# Revit family: Plumbing_Joints_Aignep_Ball-Valve-Tube-90700
name_source: partatom
category: Pipe Accessories
revit_build: Autodesk Revit 2018 (Build: 20170223_1515(x64)
units: mm (PartAtom-declared; Revit-internal decimal feet)

## family parameters
Always vertical = Yes
Cut with Voids When Loaded = No
OmniClass Number = 23.27.43.00
Part Type = Valve - Breaks Into
Round Connector Dimension = Use Diameter
Shared = No
Work Plane-Based = No

## types (6) — shared parameters
Assembly Code = D2040100
BIMobject category = Joints
Description = Ball valve tube/tube
Design country = Italy
Edition number = 1
IFC Classification = Pipe Fitting
Keynote = 15410
Lookup Table Name = Ball Valve Tube- 90705
Manufacturer = Aignep Spa
Manufacturer country = Italy
Manufacturer name = Aignep Spa
Material main = Brass
Material secondary = Aluminium
Model = 90700
OmniClass Code = 23-27 43 00
OmniClass Description = Pipe Fittings
Product Guid = ee17b265-a323-4521-a86a-9f603f37fb54
Product SKU = Ball-Valve-Tube_Tube-90700
Product certification = https://www.aignep.com
Product data url = https://www.bimobject.com
Product family = INFINITY
Product group = Valves
Product name = Ball Valve Tube/Tube- 90700
Product url = https://www.aignep.com
URL = https://www.aignep.com

## per-type parameters (varying)
- D 20: B=31.5 mm; C=58.5 mm; CH1=32 mm; CH2=30 mm; E=34.5 mm; G=88 mm; H=42 mm; H Nut 1=13.501 mm; H Nut 2=6.1 mm; H1=2.414 mm; H2=1.269 mm; H3=7.817 mm; H4=6.95 mm; I=50.7 mm; L=121.5 mm; L1=13.763 mm; M=45 mm; M Diameter 1=36.915 mm; M Diameter 2=35.623 mm; M1=17.65 mm; M2=10.874 mm  [stored 0.0356759 ft]; Nominal Diameter=20.000 mm; Nut Diameter=17 mm; QR code=https://www.bimobject.com; R=6.417 mm; Tick Size=16 mm; V1=1.768 mm; V2=3.232 mm
- D 25: B=38.5 mm; C=61.5 mm; CH1=41 mm; CH2=35 mm; E=42.5 mm; G=106 mm; H=47.5 mm; H Nut 1=4.625 mm; H Nut 2=11.6 mm; H1=4 mm  [stored 0.0131234 ft]; H2=1.342 mm; H3=8.757 mm; H4=8.547 mm; I=59.5 mm; L=138.5 mm; L1=22.115 mm; M=45 mm; M Diameter 1=43.526 mm; M Diameter 2=45 mm; M1=13.65 mm; M2=21.25 mm; Nominal Diameter=25.000 mm; Nut Diameter=21 mm; QR code=https://www.bimobject.com; R=6.417 mm; Tick Size=20 mm; V1=2.21 mm; V2=3.202 mm
- D 32: B=46 mm; C=75 mm; CH1=50 mm; CH2=45 mm; E=52 mm; G=106 mm; H=53 mm; H Nut 1=18.174 mm; H Nut 2=9.5 mm; H1=7 mm  [stored 0.0229659 ft]; H2=2.246 mm; H3=10.793 mm; H4=8.297 mm; I=65 mm; L=167 mm; L1=15.733 mm; M=45 mm; M Diameter 1=56.5 mm; M Diameter 2=55.353 mm; M1=22.5 mm; M2=14.451 mm; Nominal Diameter=32.000 mm; Nut Diameter=25.75 mm; R=6.561 mm; Tick Size=25.6 mm; V1=2.028 mm; V2=4.988 mm
- D 40: B=52.5 mm; C=81 mm; CH1=59 mm; CH2=55 mm; E=63 mm; G=134 mm; H=65 mm; H Nut 1=7.875 mm; H Nut 2=18.189 mm; H1=8.95 mm; H2=2.931 mm; H3=11.759 mm; H4=13.501 mm; I=74.5 mm; L=186 mm; L1=27.479 mm; M=47 mm; M Diameter 1=66.355 mm; M Diameter 2=68 mm; M1=16.811 mm; M2=27.75 mm; Nominal Diameter=40.000 mm; Nut Diameter=31.25 mm; R=9.041 mm; Tick Size=32 mm; V1=2.341 mm; V2=5.776 mm
- D 50: B=65 mm; C=115 mm; CH1=69 mm; CH2=74 mm; E=72.88 mm; G=134 mm; H=72.5 mm; H Nut 1=11.875 mm; H Nut 2=31.637 mm; H1=12.897 mm; H2=3.153 mm; H3=10.59 mm; H4=12.591 mm; I=82 mm; L=245 mm; L1=40.005 mm; M=47 mm; M Diameter 1=82.868 mm; M Diameter 2=84.61 mm; M1=20.363 mm; M2=40.75 mm; Nominal Diameter=50.000 mm; Nut Diameter=36.19 mm; R=8.976 mm; Tick Size=40 mm; V1=2.263 mm; V2=6.275 mm
- D 63: B=57.5 mm; C=126 mm; CH1=89 mm; CH2=75 mm; E=94 mm; G=240 mm; H=111.5 mm; H Nut 1=16.918 mm; H Nut 2=16.58 mm; H1=21.71 mm; H2=3.12 mm; H3=10.464 mm; H4=12.591 mm; I=106 mm; L=232 mm; L1=22.466 mm; M=47 mm; M Diameter 1=102.03 mm; M Diameter 2=100 mm; M1=40.92 mm; M2=41.207 mm; Nominal Diameter=63.000 mm; Nut Diameter=46.75 mm; R=8.976 mm; Tick Size=50.4 mm; V1=7.392 mm; V2=6.669 mm

note: [stored X ft] marks values corroborated as IEEE doubles in the binary element streams (Revit-internal decimal feet)

## geometry (parser evidence)
native form markers: Sweep x9
no freeform markers — native parametric forms only
